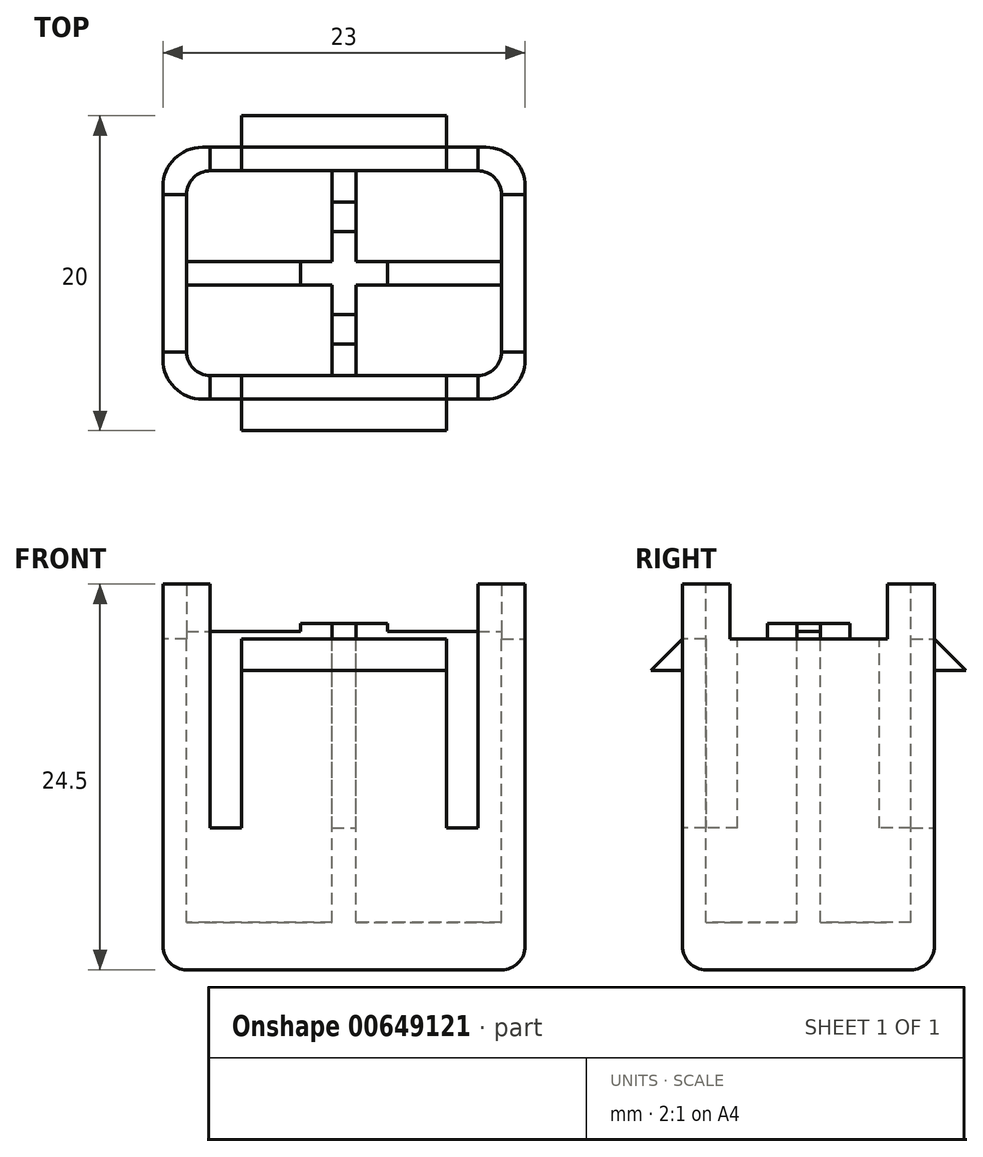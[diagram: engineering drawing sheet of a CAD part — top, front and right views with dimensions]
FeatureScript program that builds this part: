
annotation { "Feature Type Name" : "Feature", "Feature Type Description" : "" }
export const myFeature = defineFeature(function(context is Context, id is Id, definition is map)
    precondition{}
    {
        {
            var Q0;
            Q0=qCreatedBy(makeId("Top.planeOp"),FACE);
            var sketch = newSketch(context, id + "F0", { "sketchPlane" : qUnion([Q0])});
            skLineSegment(sketch, "E0.bottom", {"start": v(11.5, -8) * mm, "end": v(-11.5, -8) * mm});
            skLineSegment(sketch, "E0.top", {"start": v(11.5, 8) * mm, "end": v(-11.5, 8) * mm});
            skLineSegment(sketch, "E0.left", {"start": v(11.5, -8) * mm, "end": v(11.5, 8) * mm});
            skLineSegment(sketch, "E0.right", {"start": v(-11.5, -8) * mm, "end": v(-11.5, 8) * mm});
            skPoint(sketch, "E0.middle", {"position": v(0, 0) * mm});
            skSolve(sketch);
        }
        {
            var Q0;
            Q0=makeQuery(id+"F0.imprint","IMPRINT",FACE,{"disambiguationData":[TD([[makeQuery(id+"F0.imprint","IMPRINT",EDGE,{"derivedFrom":sQuery(id+"F0.wireOp",EDGE,"E0.bottom")}),-1.0]])]});
            extrude(context, id + "F1", {"entities" : qUnion([Q0]), "oppositeDirection" : true, "depth" : (21) * mm, "offsetDistance" : 25 * mm});
        }
        {
            var Q0;
            Q0=makeQuery(id+"F1.opExtrude","SWEPT_EDGE",EDGE,{"disambiguationData":[OSD([sQuery(id+"F0.wireOp",EDGE,"E0.bottom"),sQuery(id+"F0.wireOp",EDGE,"E0.left")])]});
            var Q1;
            Q1=makeQuery(id+"F1.opExtrude","SWEPT_EDGE",EDGE,{"disambiguationData":[OSD([sQuery(id+"F0.wireOp",EDGE,"E0.top"),sQuery(id+"F0.wireOp",EDGE,"E0.left")])]});
            var Q2;
            Q2=makeQuery(id+"F1.opExtrude","SWEPT_EDGE",EDGE,{"disambiguationData":[OSD([sQuery(id+"F0.wireOp",EDGE,"E0.bottom"),sQuery(id+"F0.wireOp",EDGE,"E0.right")])]});
            var Q3;
            Q3=makeQuery(id+"F1.opExtrude","SWEPT_EDGE",EDGE,{"disambiguationData":[OSD([sQuery(id+"F0.wireOp",EDGE,"E0.top"),sQuery(id+"F0.wireOp",EDGE,"E0.right")])]});
            fillet(context, id + "F2", {"entities" : qUnion([Q0, Q1, Q2, Q3]), "radius" : 2.5 * mm, "tangentPropagation" : true, "allowEdgeOverflow" : false});
        }
        {
            var Q0;
            Q0=makeQuery(id+"F1.opExtrude","CAP_FACE",FACE,{"disambiguationData":[OSD([sQuery(id+"F0.wireOp",EDGE,"E0.bottom"),sQuery(id+"F0.wireOp",EDGE,"E0.top"),sQuery(id+"F0.wireOp",EDGE,"E0.left"),sQuery(id+"F0.wireOp",EDGE,"E0.right")])],"isStart":true});
            var sketch = newSketch(context, id + "F3", { "sketchPlane" : qUnion([Q0])});
            skLineSegment(sketch, "E1.0", {"start": v(10, 6.5) * mm, "end": v(-10, 6.5) * mm});
            skLineSegment(sketch, "E1.1", {"start": v(10, -6.5) * mm, "end": v(10, 6.5) * mm});
            skLineSegment(sketch, "E1.2", {"start": v(10, -6.5) * mm, "end": v(-10, -6.5) * mm});
            skLineSegment(sketch, "E1.3", {"start": v(-10, -6.5) * mm, "end": v(-10, 6.5) * mm});
            skLineSegment(sketch, "E2", {"start": v(-10, 0.75) * mm, "end": v(10, 0.75) * mm});
            skLineSegment(sketch, "E3", {"start": v(-18.72, 0) * mm, "end": v(20.98, 0) * mm, "construction": true});
            skLineSegment(sketch, "E4", {"start": v(-10, -0.75) * mm, "end": v(10, -0.75) * mm});
            skLineSegment(sketch, "E5", {"start": v(-0.75, 6.5) * mm, "end": v(-0.75, -6.5) * mm});
            skLineSegment(sketch, "E6", {"start": v(0.75, 6.5) * mm, "end": v(0.75, -6.5) * mm});
            skLineSegment(sketch, "E7", {"start": v(0, 13.1) * mm, "end": v(0, -15.85) * mm, "construction": true});
            skSolve(sketch);
        }
        {
            var Q0;
            {var subQ0=sQuery(id+"F3.wireOp",EDGE,"E1.3");var subQ1=sQuery(id+"F3.wireOp",EDGE,"E1.0");var subQ2=makeQuery(id+"F3.imprint","INTERSECT",VERTEX,{"derivedFrom":[subQ1,subQ0]});Q0=makeQuery(id+"F3.imprint","IMPRINT",FACE,{"disambiguationData":[TD([[makeQuery(id+"F3.imprint","IMPRINT",EDGE,{"disambiguationData":[TD([[subQ2,1.0]])],"derivedFrom":subQ1}),1.0]])]});}
            var Q1;
            {var subQ0=sQuery(id+"F3.wireOp",EDGE,"E1.1");var subQ1=sQuery(id+"F3.wireOp",EDGE,"E1.0");var subQ2=makeQuery(id+"F3.imprint","INTERSECT",VERTEX,{"derivedFrom":[subQ1,subQ0]});Q1=makeQuery(id+"F3.imprint","IMPRINT",FACE,{"disambiguationData":[TD([[makeQuery(id+"F3.imprint","IMPRINT",EDGE,{"disambiguationData":[TD([[subQ2,-1.0]])],"derivedFrom":subQ1}),1.0]])]});}
            var Q2;
            {var subQ0=sQuery(id+"F3.wireOp",EDGE,"E1.2");var subQ1=sQuery(id+"F3.wireOp",EDGE,"E1.1");var subQ2=makeQuery(id+"F3.imprint","INTERSECT",VERTEX,{"derivedFrom":[subQ1,subQ0]});Q2=makeQuery(id+"F3.imprint","IMPRINT",FACE,{"disambiguationData":[TD([[makeQuery(id+"F3.imprint","IMPRINT",EDGE,{"disambiguationData":[TD([[subQ2,-1.0]])],"derivedFrom":subQ1}),1.0]])]});}
            var Q3;
            {var subQ0=sQuery(id+"F3.wireOp",EDGE,"E1.3");var subQ1=sQuery(id+"F3.wireOp",EDGE,"E1.2");var subQ2=makeQuery(id+"F3.imprint","INTERSECT",VERTEX,{"derivedFrom":[subQ1,subQ0]});Q3=makeQuery(id+"F3.imprint","IMPRINT",FACE,{"disambiguationData":[TD([[makeQuery(id+"F3.imprint","IMPRINT",EDGE,{"disambiguationData":[TD([[subQ2,1.0]])],"derivedFrom":subQ1}),-1.0]])]});}
            extrude(context, id + "F4", {"entities" : qUnion([Q0, Q1, Q2, Q3]), "operationType" : NewBodyOperationType.REMOVE, "oppositeDirection" : true, "depth" : (18) * mm, "offsetDistance" : 25 * mm});
        }
        {
            var Q0;
            Q0=makeQuery(id+"F4.boolean.opBoolean","COPY",EDGE,{"derivedFrom":makeQuery(id+"F4.opExtrude","SWEPT_EDGE",EDGE,{"disambiguationData":[OSD([sQuery(id+"F3.wireOp",EDGE,"E1.0"),sQuery(id+"F3.wireOp",EDGE,"E1.3")])]})});
            var Q1;
            Q1=makeQuery(id+"F4.boolean.opBoolean","COPY",EDGE,{"derivedFrom":makeQuery(id+"F4.opExtrude","SWEPT_EDGE",EDGE,{"disambiguationData":[OSD([sQuery(id+"F3.wireOp",EDGE,"E1.2"),sQuery(id+"F3.wireOp",EDGE,"E1.3")])]})});
            var Q2;
            Q2=makeQuery(id+"F4.boolean.opBoolean","COPY",EDGE,{"derivedFrom":makeQuery(id+"F4.opExtrude","SWEPT_EDGE",EDGE,{"disambiguationData":[OSD([sQuery(id+"F3.wireOp",EDGE,"E1.1"),sQuery(id+"F3.wireOp",EDGE,"E1.2")])]})});
            var Q3;
            Q3=makeQuery(id+"F4.boolean.opBoolean","COPY",EDGE,{"derivedFrom":makeQuery(id+"F4.opExtrude","SWEPT_EDGE",EDGE,{"disambiguationData":[OSD([sQuery(id+"F3.wireOp",EDGE,"E1.0"),sQuery(id+"F3.wireOp",EDGE,"E1.1")])]})});
            fillet(context, id + "F5", {"entities" : qUnion([Q0, Q1, Q2, Q3]), "radius" : 1.5 * mm, "tangentPropagation" : true, "allowEdgeOverflow" : false});
        }
        {
            var Q0;
            {var subQ0=sQuery(id+"F3.wireOp",EDGE,"E6");Q0=makeQuery(id+"F4.boolean.opBoolean","COPY",FACE,{"derivedFrom":makeQuery(id+"F4.opExtrude","SWEPT_FACE",FACE,{"disambiguationData":[OSD([subQ0]),TDD([makeQuery(id+"F3.imprint","IMPRINT",EDGE,{"disambiguationData":[TD([[makeQuery(id+"F3.imprint","INTERSECT",VERTEX,{"derivedFrom":[sQuery(id+"F3.wireOp",EDGE,"E1.0"),subQ0]}),-1.0]])],"derivedFrom":subQ0})])]})});}
            var sketch = newSketch(context, id + "F6", { "sketchPlane" : qUnion([Q0])});
            skLineSegment(sketch, "E8.0", {"start": v(6.5, -12) * mm, "end": v(6.5, 0) * mm});
            skLineSegment(sketch, "E9.0", {"start": v(4.5, -12) * mm, "end": v(4.5, 0) * mm});
            skLineSegment(sketch, "E10.0", {"start": v(6.5, -12) * mm, "end": v(4.5, -12) * mm});
            skPoint(sketch, "E11.0.end.orphan", {"position": v(0.75, -18) * mm});
            skPoint(sketch, "E12.orphan", {"position": v(6.5, -18) * mm});
            skLineSegment(sketch, "E13.0", {"start": v(-4.5, -12) * mm, "end": v(-4.5, 0) * mm});
            skLineSegment(sketch, "E14.0", {"start": v(-6.5, -12) * mm, "end": v(-6.5, 0) * mm});
            skLineSegment(sketch, "E15.0", {"start": v(-4.5, -12) * mm, "end": v(-6.5, -12) * mm});
            skLineSegment(sketch, "E16", {"start": v(-6.5, 0) * mm, "end": v(-4.5, 0) * mm});
            skLineSegment(sketch, "E17", {"start": v(4.5, 0) * mm, "end": v(6.5, 0) * mm});
            skSolve(sketch);
        }
        {
            var Q0;
            Q0=makeQuery(id+"F6.imprint","IMPRINT",FACE,{"disambiguationData":[TD([[makeQuery(id+"F6.imprint","IMPRINT",EDGE,{"derivedFrom":sQuery(id+"F6.wireOp",EDGE,"E13.0")}),1.0]])]});
            var Q1;
            Q1=makeQuery(id+"F6.imprint","IMPRINT",FACE,{"disambiguationData":[TD([[makeQuery(id+"F6.imprint","IMPRINT",EDGE,{"derivedFrom":sQuery(id+"F6.wireOp",EDGE,"E8.0")}),1.0]])]});
            var Q2;
            {var subQ0=sQuery(id+"F3.wireOp",EDGE,"E5");Q2=makeQuery(id+"F4.boolean.opBoolean","COPY",FACE,{"derivedFrom":makeQuery(id+"F4.opExtrude","SWEPT_FACE",FACE,{"disambiguationData":[OSD([subQ0]),TDD([makeQuery(id+"F3.imprint","IMPRINT",EDGE,{"disambiguationData":[TD([[makeQuery(id+"F3.imprint","INTERSECT",VERTEX,{"derivedFrom":[sQuery(id+"F3.wireOp",EDGE,"E1.0"),subQ0]}),-1.0]])],"derivedFrom":subQ0})])]})});}
            extrude(context, id + "F7", {"entities" : qUnion([Q0, Q1]), "operationType" : NewBodyOperationType.REMOVE, "endBound" : BoundingType.UP_TO_SURFACE, "oppositeDirection" : true, "depth" : 25 * mm, "endBoundEntityFace" : qUnion([Q2]), "offsetDistance" : 25 * mm});
        }
        {
            var Q0;
            Q0=makeQuery(id+"F1.opExtrude","SWEPT_FACE",FACE,{"disambiguationData":[OSD([sQuery(id+"F0.wireOp",EDGE,"E0.top")])]});
            var sketch = newSketch(context, id + "F8", { "sketchPlane" : qUnion([Q0])});
            skLineSegment(sketch, "E18.bottom", {"start": v(6.5, 0) * mm, "end": v(8.5, 0) * mm});
            skLineSegment(sketch, "E18.top", {"start": v(6.5, -12) * mm, "end": v(8.5, -12) * mm});
            skLineSegment(sketch, "E18.left", {"start": v(6.5, 0) * mm, "end": v(6.5, -12) * mm});
            skLineSegment(sketch, "E18.right", {"start": v(8.5, 0) * mm, "end": v(8.5, -12) * mm});
            skLineSegment(sketch, "E19.bottom", {"start": v(-8.5, 0) * mm, "end": v(-6.5, 0) * mm});
            skLineSegment(sketch, "E19.top", {"start": v(-8.5, -12) * mm, "end": v(-6.5, -12) * mm});
            skLineSegment(sketch, "E19.left", {"start": v(-8.5, 0) * mm, "end": v(-8.5, -12) * mm});
            skLineSegment(sketch, "E19.right", {"start": v(-6.5, 0) * mm, "end": v(-6.5, -12) * mm});
            skSolve(sketch);
        }
        {
            var Q0;
            Q0=makeQuery(id+"F8.imprint","IMPRINT",FACE,{"disambiguationData":[TD([[makeQuery(id+"F8.imprint","IMPRINT",EDGE,{"derivedFrom":sQuery(id+"F8.wireOp",EDGE,"E18.bottom")}),-1.0]])]});
            var Q1;
            Q1=makeQuery(id+"F8.imprint","IMPRINT",FACE,{"disambiguationData":[TD([[makeQuery(id+"F8.imprint","IMPRINT",EDGE,{"derivedFrom":sQuery(id+"F8.wireOp",EDGE,"E19.bottom")}),-1.0]])]});
            var Q2;
            {var subQ0=sQuery(id+"F3.wireOp",EDGE,"E1.0");Q2=makeQuery(id+"F7.boolean.opBoolean","MERGE",FACE,{"derivedFrom":[makeQuery(id+"F4.boolean.opBoolean","COPY",FACE,{"derivedFrom":makeQuery(id+"F4.opExtrude","SWEPT_FACE",FACE,{"disambiguationData":[OSD([subQ0]),TDD([makeQuery(id+"F3.imprint","IMPRINT",EDGE,{"disambiguationData":[TD([[makeQuery(id+"F3.imprint","INTERSECT",VERTEX,{"derivedFrom":[subQ0,sQuery(id+"F3.wireOp",EDGE,"E1.1")]}),-1.0]])],"derivedFrom":subQ0})])]})}),makeQuery(id+"F4.boolean.opBoolean","COPY",FACE,{"derivedFrom":makeQuery(id+"F4.opExtrude","SWEPT_FACE",FACE,{"disambiguationData":[OSD([subQ0]),TDD([makeQuery(id+"F3.imprint","IMPRINT",EDGE,{"disambiguationData":[TD([[makeQuery(id+"F3.imprint","INTERSECT",VERTEX,{"derivedFrom":[subQ0,sQuery(id+"F3.wireOp",EDGE,"E1.3")]}),1.0]])],"derivedFrom":subQ0})])]})}),makeQuery(id+"F7.opExtrude","SWEPT_FACE",FACE,{"disambiguationData":[OSD([sQuery(id+"F6.wireOp",EDGE,"E8.0")])]})]});}
            var Q3;
            {var subQ0=sQuery(id+"F3.wireOp",EDGE,"E1.0");Q3=makeQuery(id+"F7.boolean.opBoolean","MERGE",FACE,{"derivedFrom":[makeQuery(id+"F4.boolean.opBoolean","COPY",FACE,{"derivedFrom":makeQuery(id+"F4.opExtrude","SWEPT_FACE",FACE,{"disambiguationData":[OSD([subQ0]),TDD([makeQuery(id+"F3.imprint","IMPRINT",EDGE,{"disambiguationData":[TD([[makeQuery(id+"F3.imprint","INTERSECT",VERTEX,{"derivedFrom":[subQ0,sQuery(id+"F3.wireOp",EDGE,"E1.1")]}),-1.0]])],"derivedFrom":subQ0})])]})}),makeQuery(id+"F4.boolean.opBoolean","COPY",FACE,{"derivedFrom":makeQuery(id+"F4.opExtrude","SWEPT_FACE",FACE,{"disambiguationData":[OSD([subQ0]),TDD([makeQuery(id+"F3.imprint","IMPRINT",EDGE,{"disambiguationData":[TD([[makeQuery(id+"F3.imprint","INTERSECT",VERTEX,{"derivedFrom":[subQ0,sQuery(id+"F3.wireOp",EDGE,"E1.3")]}),1.0]])],"derivedFrom":subQ0})])]})}),makeQuery(id+"F7.opExtrude","SWEPT_FACE",FACE,{"disambiguationData":[OSD([sQuery(id+"F6.wireOp",EDGE,"E8.0")])]})]});}
            extrude(context, id + "F9", {"entities" : qUnion([Q0, Q1, Q2]), "operationType" : NewBodyOperationType.REMOVE, "endBound" : BoundingType.UP_TO_NEXT, "oppositeDirection" : true, "depth" : 25 * mm, "endBoundEntityFace" : qUnion([Q3]), "offsetDistance" : 25 * mm});
        }
        {
            var Q0;
            Q0=makeQuery(id+"F1.opExtrude","SWEPT_FACE",FACE,{"disambiguationData":[OSD([sQuery(id+"F0.wireOp",EDGE,"E0.bottom")])]});
            var sketch = newSketch(context, id + "F10", { "sketchPlane" : qUnion([Q0])});
            skLineSegment(sketch, "E20.bottom", {"start": v(-8.5, 0) * mm, "end": v(-6.5, 0) * mm});
            skLineSegment(sketch, "E20.top", {"start": v(-8.5, -12) * mm, "end": v(-6.5, -12) * mm});
            skLineSegment(sketch, "E20.left", {"start": v(-8.5, 0) * mm, "end": v(-8.5, -12) * mm});
            skLineSegment(sketch, "E20.right", {"start": v(-6.5, 0) * mm, "end": v(-6.5, -12) * mm});
            skLineSegment(sketch, "E21.bottom", {"start": v(6.5, 0) * mm, "end": v(8.5, 0) * mm});
            skLineSegment(sketch, "E21.top", {"start": v(6.5, -12) * mm, "end": v(8.5, -12) * mm});
            skLineSegment(sketch, "E21.left", {"start": v(6.5, 0) * mm, "end": v(6.5, -12) * mm});
            skLineSegment(sketch, "E21.right", {"start": v(8.5, 0) * mm, "end": v(8.5, -12) * mm});
            skSolve(sketch);
        }
        {
            var Q0;
            Q0=makeQuery(id+"F10.imprint","IMPRINT",FACE,{"disambiguationData":[TD([[makeQuery(id+"F10.imprint","IMPRINT",EDGE,{"derivedFrom":sQuery(id+"F10.wireOp",EDGE,"E20.bottom")}),1.0]])]});
            var Q1;
            Q1=makeQuery(id+"F10.imprint","IMPRINT",FACE,{"disambiguationData":[TD([[makeQuery(id+"F10.imprint","IMPRINT",EDGE,{"derivedFrom":sQuery(id+"F10.wireOp",EDGE,"E21.bottom")}),1.0]])]});
            extrude(context, id + "F11", {"entities" : qUnion([Q0, Q1]), "operationType" : NewBodyOperationType.REMOVE, "endBound" : BoundingType.UP_TO_NEXT, "oppositeDirection" : true, "depth" : 25 * mm, "offsetDistance" : 25 * mm});
        }
        {
            var Q0;
            Q0=makeQuery(id+"F11.boolean.opBoolean","COPY",FACE,{"derivedFrom":makeQuery(id+"F11.opExtrude","SWEPT_FACE",FACE,{"disambiguationData":[OSD([sQuery(id+"F10.wireOp",EDGE,"E20.right")])]})});
            var sketch = newSketch(context, id + "F12", { "sketchPlane" : qUnion([Q0])});
            skLineSegment(sketch, "E22", {"start": v(10, -2) * mm, "end": v(8, -2) * mm});
            skLineSegment(sketch, "E23", {"start": v(8, -2) * mm, "end": v(8, 0) * mm});
            skLineSegment(sketch, "E24", {"start": v(-8, 0) * mm, "end": v(-8, -2) * mm});
            skLineSegment(sketch, "E25", {"start": v(-8, -2) * mm, "end": v(-10, -2) * mm});
            skLineSegment(sketch, "E26", {"start": v(-8, 0) * mm, "end": v(-10, -2) * mm});
            skLineSegment(sketch, "E27", {"start": v(8, 0) * mm, "end": v(10, -2) * mm});
            skSolve(sketch);
        }
        {
            var Q0;
            {var subQ9=sQuery(id+"F0.wireOp",EDGE,"E0.top");var subQ10=makeQuery(id+"F1.opExtrude","SWEPT_FACE",FACE,{"disambiguationData":[OSD([subQ9])]});var subQ20=sQuery(id+"F0.wireOp",EDGE,"E0.bottom");var subQ21=makeQuery(id+"F1.opExtrude","SWEPT_FACE",FACE,{"disambiguationData":[OSD([subQ20])]});var subQ27=sQuery(id+"F0.wireOp",EDGE,"E0.left");var subQ36=sQuery(id+"F0.wireOp",EDGE,"E0.right");Q0=makeQuery(id+"F11.boolean.opBoolean","SPLIT",FACE,{"disambiguationData":[TD([subQ10])],"derivedFrom":makeQuery(id+"F9.boolean.opBoolean","SPLIT",FACE,{"disambiguationData":[TD([subQ21])],"derivedFrom":makeQuery(id+"F1.opExtrude","CAP_FACE",FACE,{"disambiguationData":[OSD([subQ20,subQ9,subQ27,subQ36])],"isStart":true})})});}
            var sketch = newSketch(context, id + "F13", { "sketchPlane" : qUnion([Q0])});
            skLineSegment(sketch, "E28.bottom", {"start": v(-10, 5) * mm, "end": v(-11.5, 5) * mm});
            skLineSegment(sketch, "E28.top", {"start": v(-10, -5) * mm, "end": v(-11.5, -5) * mm});
            skLineSegment(sketch, "E28.left", {"start": v(-10, 5) * mm, "end": v(-10, -5) * mm});
            skLineSegment(sketch, "E28.right", {"start": v(-11.5, 5) * mm, "end": v(-11.5, -5) * mm});
            skLineSegment(sketch, "E29.bottom", {"start": v(10, 5) * mm, "end": v(11.5, 5) * mm});
            skLineSegment(sketch, "E29.top", {"start": v(10, -5) * mm, "end": v(11.5, -5) * mm});
            skLineSegment(sketch, "E29.left", {"start": v(10, 5) * mm, "end": v(10, -5) * mm});
            skLineSegment(sketch, "E29.right", {"start": v(11.5, 5) * mm, "end": v(11.5, -5) * mm});
            skSolve(sketch);
        }
        {
            var Q0;
            {var subQ8=sQuery(id+"F13.wireOp",EDGE,"E28.bottom");Q0=makeQuery(id+"F13.imprint","IMPRINT",FACE,{"disambiguationData":[TD([[makeQuery(id+"F13.imprint","IMPRINT",EDGE,{"derivedFrom":subQ8}),-1.0]])]});}
            var Q1;
            {var subQ8=sQuery(id+"F13.wireOp",EDGE,"E28.top");Q1=makeQuery(id+"F13.imprint","IMPRINT",FACE,{"disambiguationData":[TD([[makeQuery(id+"F13.imprint","IMPRINT",EDGE,{"derivedFrom":subQ8}),1.0]])]});}
            var Q2;
            {var subQ8=sQuery(id+"F13.wireOp",EDGE,"E29.top");Q2=makeQuery(id+"F13.imprint","IMPRINT",FACE,{"disambiguationData":[TD([[makeQuery(id+"F13.imprint","IMPRINT",EDGE,{"derivedFrom":subQ8}),-1.0]])]});}
            var Q3;
            {var subQ2=sQuery(id+"F13.wireOp",EDGE,"E29.bottom");Q3=makeQuery(id+"F13.imprint","IMPRINT",FACE,{"disambiguationData":[TD([[makeQuery(id+"F13.imprint","IMPRINT",EDGE,{"derivedFrom":subQ2}),1.0]])]});}
            extrude(context, id + "F14", {"entities" : qUnion([Q0, Q1, Q2, Q3]), "operationType" : NewBodyOperationType.ADD, "depth" : 3.5 * mm, "offsetDistance" : 25 * mm});
        }
        {
            var Q0;
            {var subQ9=sQuery(id+"F0.wireOp",EDGE,"E0.top");var subQ10=makeQuery(id+"F1.opExtrude","SWEPT_FACE",FACE,{"disambiguationData":[OSD([subQ9])]});var subQ20=sQuery(id+"F0.wireOp",EDGE,"E0.bottom");var subQ21=makeQuery(id+"F1.opExtrude","SWEPT_FACE",FACE,{"disambiguationData":[OSD([subQ20])]});var subQ27=sQuery(id+"F0.wireOp",EDGE,"E0.left");var subQ36=sQuery(id+"F0.wireOp",EDGE,"E0.right");Q0=makeQuery(id+"F11.boolean.opBoolean","SPLIT",FACE,{"disambiguationData":[TD([subQ10])],"derivedFrom":makeQuery(id+"F9.boolean.opBoolean","SPLIT",FACE,{"disambiguationData":[TD([subQ21])],"derivedFrom":makeQuery(id+"F1.opExtrude","CAP_FACE",FACE,{"disambiguationData":[OSD([subQ20,subQ9,subQ27,subQ36])],"isStart":true})})});}
            var sketch = newSketch(context, id + "F15", { "sketchPlane" : qUnion([Q0])});
            skLineSegment(sketch, "E30", {"start": v(-10, 0.75) * mm, "end": v(-10, -0.75) * mm});
            skLineSegment(sketch, "E31", {"start": v(10, 0.75) * mm, "end": v(10, -0.75) * mm});
            skLineSegment(sketch, "E32", {"start": v(-2.75, 0.75) * mm, "end": v(-2.75, -0.75) * mm});
            skLineSegment(sketch, "E33", {"start": v(-0.75, 2.62) * mm, "end": v(0.75, 2.62) * mm});
            skLineSegment(sketch, "E34", {"start": v(2.75, 0.75) * mm, "end": v(2.75, -0.75) * mm});
            skLineSegment(sketch, "E35", {"start": v(-0.75, -2.62) * mm, "end": v(0.75, -2.62) * mm});
            skSolve(sketch);
        }
        {
            var Q0;
            {var subQ23=sQuery(id+"F15.wireOp",EDGE,"E32");Q0=makeQuery(id+"F15.imprint","IMPRINT",FACE,{"disambiguationData":[TD([[makeQuery(id+"F15.imprint","IMPRINT",EDGE,{"derivedFrom":subQ23}),1.0]])]});}
            extrude(context, id + "F16", {"entities" : qUnion([Q0]), "operationType" : NewBodyOperationType.ADD, "depth" : (1) * mm, "offsetDistance" : 25 * mm});
        }
        {
            var Q0;
            {var subQ15=sQuery(id+"F0.wireOp",EDGE,"E0.left");var subQ17=sQuery(id+"F0.wireOp",EDGE,"E0.right");var subQ18=sQuery(id+"F0.wireOp",EDGE,"E0.top");var subQ19=sQuery(id+"F0.wireOp",EDGE,"E0.bottom");var subQ20=makeQuery(id+"F1.opExtrude","CAP_FACE",FACE,{"disambiguationData":[OSD([subQ19,subQ18,subQ15,subQ17])],"isStart":true});var subQ22=makeQuery(id+"F1.opExtrude","SWEPT_FACE",FACE,{"disambiguationData":[OSD([subQ15])]});var subQ26=subQ20;var subQ37=makeQuery(id+"F1.opExtrude","SWEPT_FACE",FACE,{"disambiguationData":[OSD([subQ18])]});var subQ45=makeQuery(id+"F1.opExtrude","SWEPT_FACE",FACE,{"disambiguationData":[OSD([subQ19])]});Q0=makeQuery(id+"F16.boolean.opBoolean","SPLIT",FACE,{"disambiguationData":[TD([subQ22])],"derivedFrom":makeQuery(id+"F11.boolean.opBoolean","SPLIT",FACE,{"disambiguationData":[TD([subQ37])],"derivedFrom":makeQuery(id+"F9.boolean.opBoolean","SPLIT",FACE,{"disambiguationData":[TD([subQ45])],"derivedFrom":subQ26})})});}
            var sketch = newSketch(context, id + "F17", { "sketchPlane" : qUnion([Q0])});
            skLineSegment(sketch, "E36.bottom", {"start": v(2.75, -0.75) * mm, "end": v(10, -0.75) * mm});
            skLineSegment(sketch, "E36.top", {"start": v(2.75, 0.75) * mm, "end": v(10, 0.75) * mm});
            skLineSegment(sketch, "E36.left", {"start": v(2.75, -0.75) * mm, "end": v(2.75, 0.75) * mm});
            skLineSegment(sketch, "E36.right", {"start": v(10, -0.75) * mm, "end": v(10, 0.75) * mm});
            skSolve(sketch);
        }
        {
            var Q0;
            {var subQ19=sQuery(id+"F0.wireOp",EDGE,"E0.right");var subQ21=sQuery(id+"F0.wireOp",EDGE,"E0.left");var subQ22=sQuery(id+"F0.wireOp",EDGE,"E0.top");var subQ23=sQuery(id+"F0.wireOp",EDGE,"E0.bottom");var subQ24=makeQuery(id+"F1.opExtrude","CAP_FACE",FACE,{"disambiguationData":[OSD([subQ23,subQ22,subQ21,subQ19])],"isStart":true});var subQ27=makeQuery(id+"F1.opExtrude","SWEPT_FACE",FACE,{"disambiguationData":[OSD([subQ19])]});var subQ29=subQ24;var subQ42=makeQuery(id+"F1.opExtrude","SWEPT_FACE",FACE,{"disambiguationData":[OSD([subQ22])]});var subQ47=makeQuery(id+"F1.opExtrude","SWEPT_FACE",FACE,{"disambiguationData":[OSD([subQ23])]});Q0=makeQuery(id+"F16.boolean.opBoolean","SPLIT",FACE,{"disambiguationData":[TD([subQ27])],"derivedFrom":makeQuery(id+"F11.boolean.opBoolean","SPLIT",FACE,{"disambiguationData":[TD([subQ42])],"derivedFrom":makeQuery(id+"F9.boolean.opBoolean","SPLIT",FACE,{"disambiguationData":[TD([subQ47])],"derivedFrom":subQ29})})});}
            var sketch = newSketch(context, id + "F18", { "sketchPlane" : qUnion([Q0])});
            skLineSegment(sketch, "E37.bottom", {"start": v(-2.75, -0.75) * mm, "end": v(-10, -0.75) * mm});
            skLineSegment(sketch, "E37.top", {"start": v(-2.75, 0.75) * mm, "end": v(-10, 0.75) * mm});
            skLineSegment(sketch, "E37.left", {"start": v(-2.75, -0.75) * mm, "end": v(-2.75, 0.75) * mm});
            skLineSegment(sketch, "E37.right", {"start": v(-10, -0.75) * mm, "end": v(-10, 0.75) * mm});
            skSolve(sketch);
        }
        {
            var Q0;
            Q0=makeQuery(id+"F18.imprint","IMPRINT",FACE,{"disambiguationData":[TD([[makeQuery(id+"F18.imprint","IMPRINT",EDGE,{"derivedFrom":sQuery(id+"F18.wireOp",EDGE,"E37.bottom")}),1.0]])]});
            var Q1;
            Q1=makeQuery(id+"F17.imprint","IMPRINT",FACE,{"disambiguationData":[TD([[makeQuery(id+"F17.imprint","IMPRINT",EDGE,{"derivedFrom":sQuery(id+"F17.wireOp",EDGE,"E36.bottom")}),1.0]])]});
            extrude(context, id + "F19", {"entities" : qUnion([Q0, Q1]), "operationType" : NewBodyOperationType.ADD, "depth" : .5 * mm, "offsetDistance" : 25 * mm});
        }
        {
            var Q0;
            Q0=makeQuery(id+"F1.opExtrude","CAP_EDGE",EDGE,{"disambiguationData":[OSD([sQuery(id+"F0.wireOp",EDGE,"E0.left")])],"isStart":false});
            var Q1;
            {var subQ0=sQuery(id+"F0.wireOp",EDGE,"E0.left");var subQ1=sQuery(id+"F0.wireOp",EDGE,"E0.top");Q1=makeQuery(id+"F2.opFillet","BLEND_EDGE",EDGE,{"blendedFrom":[makeQuery(id+"F1.opExtrude","SWEPT_EDGE",EDGE,{"disambiguationData":[OSD([subQ1,subQ0])]}),makeQuery(id+"F1.opExtrude","CAP_FACE",FACE,{"disambiguationData":[OSD([sQuery(id+"F0.wireOp",EDGE,"E0.bottom"),subQ1,subQ0,sQuery(id+"F0.wireOp",EDGE,"E0.right")])],"isStart":false})],"blendedInto":[makeQuery(id+"F1.opExtrude","CAP_FACE",FACE,{"disambiguationData":[OSD([sQuery(id+"F0.wireOp",EDGE,"E0.bottom"),subQ1,subQ0,sQuery(id+"F0.wireOp",EDGE,"E0.right")])],"isStart":false})]});}
            var Q2;
            Q2=makeQuery(id+"F1.opExtrude","CAP_EDGE",EDGE,{"disambiguationData":[OSD([sQuery(id+"F0.wireOp",EDGE,"E0.top")])],"isStart":false});
            var Q3;
            {var subQ0=sQuery(id+"F0.wireOp",EDGE,"E0.right");var subQ1=sQuery(id+"F0.wireOp",EDGE,"E0.top");Q3=makeQuery(id+"F2.opFillet","BLEND_EDGE",EDGE,{"blendedFrom":[makeQuery(id+"F1.opExtrude","SWEPT_EDGE",EDGE,{"disambiguationData":[OSD([subQ1,subQ0])]}),makeQuery(id+"F1.opExtrude","CAP_FACE",FACE,{"disambiguationData":[OSD([sQuery(id+"F0.wireOp",EDGE,"E0.bottom"),subQ1,sQuery(id+"F0.wireOp",EDGE,"E0.left"),subQ0])],"isStart":false})],"blendedInto":[makeQuery(id+"F1.opExtrude","CAP_FACE",FACE,{"disambiguationData":[OSD([sQuery(id+"F0.wireOp",EDGE,"E0.bottom"),subQ1,sQuery(id+"F0.wireOp",EDGE,"E0.left"),subQ0])],"isStart":false})]});}
            var Q4;
            Q4=makeQuery(id+"F1.opExtrude","CAP_EDGE",EDGE,{"disambiguationData":[OSD([sQuery(id+"F0.wireOp",EDGE,"E0.right")])],"isStart":false});
            var Q5;
            {var subQ0=sQuery(id+"F0.wireOp",EDGE,"E0.right");var subQ1=sQuery(id+"F0.wireOp",EDGE,"E0.bottom");Q5=makeQuery(id+"F2.opFillet","BLEND_EDGE",EDGE,{"blendedFrom":[makeQuery(id+"F1.opExtrude","SWEPT_EDGE",EDGE,{"disambiguationData":[OSD([subQ1,subQ0])]}),makeQuery(id+"F1.opExtrude","CAP_FACE",FACE,{"disambiguationData":[OSD([subQ1,sQuery(id+"F0.wireOp",EDGE,"E0.top"),sQuery(id+"F0.wireOp",EDGE,"E0.left"),subQ0])],"isStart":false})],"blendedInto":[makeQuery(id+"F1.opExtrude","CAP_FACE",FACE,{"disambiguationData":[OSD([subQ1,sQuery(id+"F0.wireOp",EDGE,"E0.top"),sQuery(id+"F0.wireOp",EDGE,"E0.left"),subQ0])],"isStart":false})]});}
            var Q6;
            Q6=makeQuery(id+"F1.opExtrude","CAP_EDGE",EDGE,{"disambiguationData":[OSD([sQuery(id+"F0.wireOp",EDGE,"E0.bottom")])],"isStart":false});
            var Q7;
            {var subQ0=sQuery(id+"F0.wireOp",EDGE,"E0.left");var subQ1=sQuery(id+"F0.wireOp",EDGE,"E0.bottom");Q7=makeQuery(id+"F2.opFillet","BLEND_EDGE",EDGE,{"blendedFrom":[makeQuery(id+"F1.opExtrude","SWEPT_EDGE",EDGE,{"disambiguationData":[OSD([subQ1,subQ0])]}),makeQuery(id+"F1.opExtrude","CAP_FACE",FACE,{"disambiguationData":[OSD([subQ1,sQuery(id+"F0.wireOp",EDGE,"E0.top"),subQ0,sQuery(id+"F0.wireOp",EDGE,"E0.right")])],"isStart":false})],"blendedInto":[makeQuery(id+"F1.opExtrude","CAP_FACE",FACE,{"disambiguationData":[OSD([subQ1,sQuery(id+"F0.wireOp",EDGE,"E0.top"),subQ0,sQuery(id+"F0.wireOp",EDGE,"E0.right")])],"isStart":false})]});}
            fillet(context, id + "F20", {"entities" : qUnion([Q0, Q1, Q2, Q3, Q4, Q5, Q6, Q7]), "radius" : 1.5 * mm, "tangentPropagation" : true, "allowEdgeOverflow" : false});
        }
        {
            var Q0;
            Q0=makeQuery(id+"F12.imprint","IMPRINT",FACE,{"disambiguationData":[TD([[makeQuery(id+"F12.imprint","IMPRINT",EDGE,{"derivedFrom":sQuery(id+"F12.wireOp",EDGE,"E24")}),-1.0]])]});
            var Q1;
            Q1=makeQuery(id+"F12.imprint","IMPRINT",FACE,{"disambiguationData":[TD([[makeQuery(id+"F12.imprint","IMPRINT",EDGE,{"derivedFrom":sQuery(id+"F12.wireOp",EDGE,"E22")}),-1.0]])]});
            var Q2;
            Q2=makeQuery(id+"F9.boolean.opBoolean","COPY",FACE,{"derivedFrom":makeQuery(id+"F9.opExtrude","SWEPT_FACE",FACE,{"disambiguationData":[OSD([sQuery(id+"F8.wireOp",EDGE,"E19.right")])]})});
            extrude(context, id + "F21", {"entities" : qUnion([Q0, Q1]), "operationType" : NewBodyOperationType.ADD, "endBound" : BoundingType.UP_TO_SURFACE, "oppositeDirection" : true, "depth" : 25 * mm, "endBoundEntityFace" : qUnion([Q2]), "offsetDistance" : 25 * mm});
        }
    });
